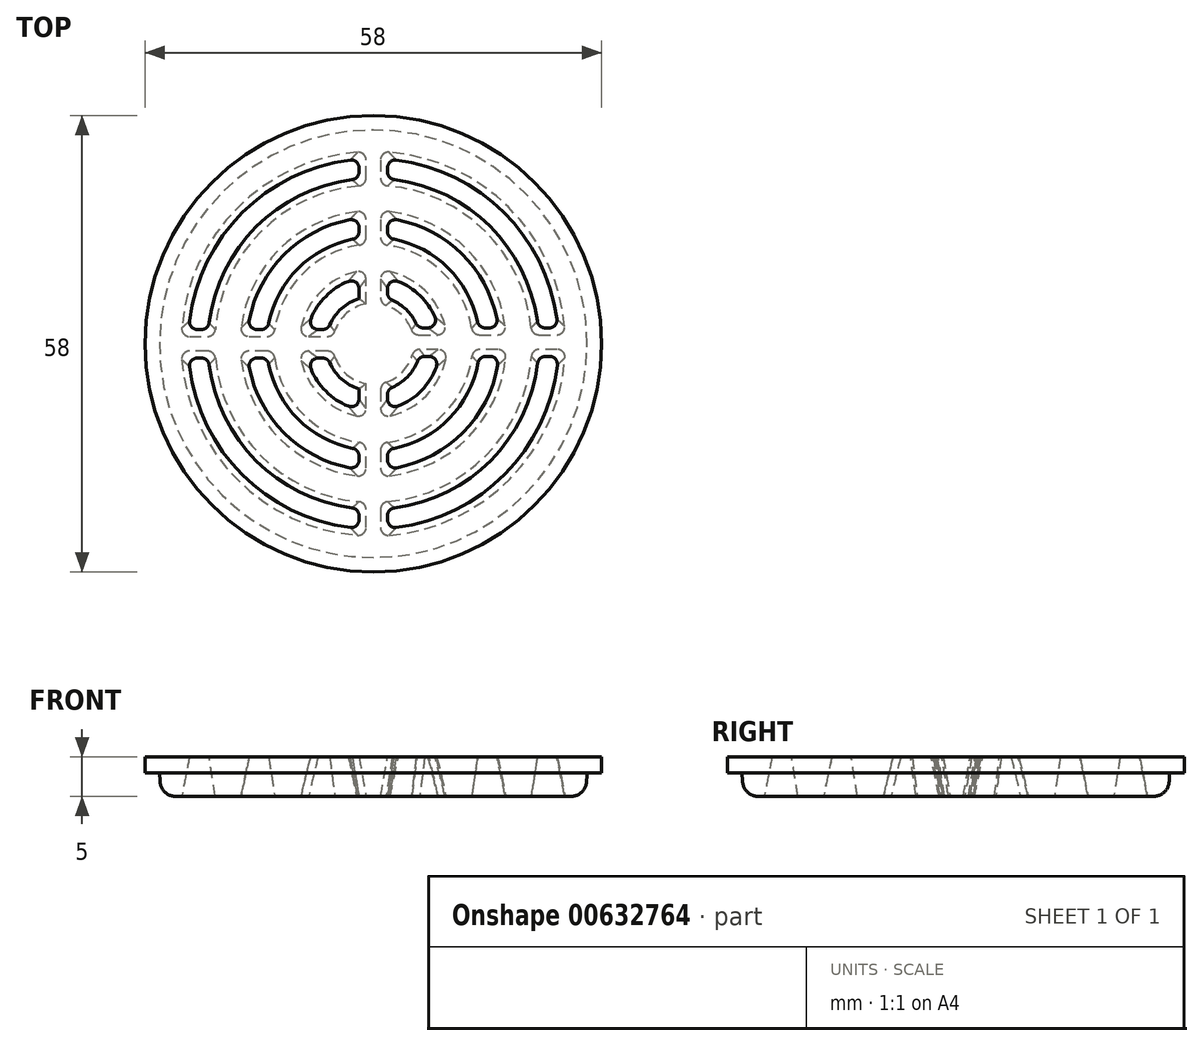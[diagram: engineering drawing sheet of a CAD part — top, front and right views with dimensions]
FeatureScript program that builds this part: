
annotation { "Feature Type Name" : "Feature", "Feature Type Description" : "" }
export const myFeature = defineFeature(function(context is Context, id is Id, definition is map)
    precondition{}
    {
        {
            var Q0;
            Q0=qCreatedBy(makeId("Top.planeOp"),FACE);
            var sketch = newSketch(context, id + "F0", { "sketchPlane" : qUnion([Q0])});
            skCircle(sketch, "E0", {"center": v(0, 0) * mm, "radius": 27 * mm});
            skSolve(sketch);
        }
        {
            var Q0;
            Q0=makeQuery(id+"F0.imprint","IMPRINT",FACE,{"disambiguationData":[TD([[makeQuery(id+"F0.imprint","IMPRINT",EDGE,{"derivedFrom":sQuery(id+"F0.wireOp",EDGE,"E0")}),1.0]])]});
            extrude(context, id + "F1", {"entities" : qUnion([Q0]), "depth" : 3 * mm, "offsetDistance" : 25 * mm, "hasDraft" : true, "draftAngle" : 3 * degree});
        }
        {
            var Q0;
            Q0=makeQuery(id+"F1.opExtrude","CAP_FACE",FACE,{"disambiguationData":[OSD([sQuery(id+"F0.wireOp",EDGE,"E0")])],"isStart":false});
            var sketch = newSketch(context, id + "F2", { "sketchPlane" : qUnion([Q0])});
            skCircle(sketch, "E1", {"center": v(0, 0) * mm, "radius": 29 * mm});
            skSolve(sketch);
        }
        {
            var Q0;
            Q0 = qSketchRegion(id + "F2", true);
            extrude(context, id + "F3", {"entities" : qUnion([Q0]), "operationType" : NewBodyOperationType.ADD, "depth" : 2 * mm, "offsetDistance" : 25 * mm});
        }
        {
            var Q0;
            Q0=makeQuery(id+"F3.opExtrude","CAP_FACE",FACE,{"disambiguationData":[OSD([sQuery(id+"F2.wireOp",EDGE,"E1")])],"isStart":false});
            var sketch = newSketch(context, id + "F4", { "sketchPlane" : qUnion([Q0])});
            skArc(sketch, "E2", {"start": v(5.68, 2.02) * mm, "mid": v(4.18, 4.34) * mm, "end": v(1.81, 5.75) * mm});
            skArc(sketch, "E3", {"start": v(8.29, 2.02) * mm, "mid": v(5.95, 6.1) * mm, "end": v(1.81, 8.33) * mm});
            skArc(sketch, "E4", {"start": v(13.38, 2.02) * mm, "mid": v(9.5, 9.64) * mm, "end": v(1.81, 13.4) * mm});
            skArc(sketch, "E5", {"start": v(15.9, 2.02) * mm, "mid": v(11.26, 11.4) * mm, "end": v(1.81, 15.93) * mm});
            skArc(sketch, "E6", {"start": v(1.81, -23.46) * mm, "mid": v(16.71, -16.56) * mm, "end": v(23.47, -1.6) * mm});
            skArc(sketch, "E7", {"start": v(20.93, 2.02) * mm, "mid": v(14.8, 14.94) * mm, "end": v(1.81, 20.95) * mm});
            skLineSegment(sketch, "E8.left", {"start": v(-1.81, 15.93) * mm, "end": v(-1.81, 13.4) * mm});
            skLineSegment(sketch, "E8.right", {"start": v(1.81, 15.93) * mm, "end": v(1.81, 13.4) * mm});
            skLineSegment(sketch, "E9.bottom", {"start": v(-5.75, 1.81) * mm, "end": v(-8.33, 1.81) * mm});
            skLineSegment(sketch, "E9.top", {"start": v(-5.75, -1.81) * mm, "end": v(-8.33, -1.81) * mm});
            skLineSegment(sketch, "E10.left", {"start": v(-1.81, -5.75) * mm, "end": v(-1.81, -8.33) * mm});
            skLineSegment(sketch, "E10.right", {"start": v(1.81, -5.75) * mm, "end": v(1.81, -8.33) * mm});
            skLineSegment(sketch, "E11.bottom", {"start": v(5.81, -1.6) * mm, "end": v(8.38, -1.6) * mm});
            skLineSegment(sketch, "E11.top", {"start": v(5.68, 2.02) * mm, "end": v(8.29, 2.02) * mm});
            skArc(sketch, "E12.trimOffspring", {"start": v(1.81, -20.95) * mm, "mid": v(14.94, -14.8) * mm, "end": v(20.97, -1.6) * mm});
            skArc(sketch, "E13.trimOffspring", {"start": v(1.81, -15.93) * mm, "mid": v(11.4, -11.26) * mm, "end": v(15.95, -1.6) * mm});
            skArc(sketch, "E14.trimOffspring", {"start": v(1.81, -13.4) * mm, "mid": v(9.64, -9.5) * mm, "end": v(13.43, -1.6) * mm});
            skArc(sketch, "E15.trimOffspring", {"start": v(1.81, -8.33) * mm, "mid": v(6.1, -5.95) * mm, "end": v(8.38, -1.6) * mm});
            skArc(sketch, "E16.trimOffspring", {"start": v(1.81, -5.75) * mm, "mid": v(4.34, -4.19) * mm, "end": v(5.81, -1.6) * mm});
            skLineSegment(sketch, "E17.trimOffspring", {"start": v(1.81, -13.4) * mm, "end": v(1.81, -15.93) * mm});
            skLineSegment(sketch, "E18.trimOffspring", {"start": v(-1.81, -13.4) * mm, "end": v(-1.81, -15.93) * mm});
            skLineSegment(sketch, "E19.trimOffspring", {"start": v(-1.81, -20.95) * mm, "end": v(-1.81, -23.46) * mm});
            skLineSegment(sketch, "E20.trimOffspring", {"start": v(1.81, -20.95) * mm, "end": v(1.81, -23.46) * mm});
            skLineSegment(sketch, "E21.trimOffspring", {"start": v(13.43, -1.6) * mm, "end": v(15.95, -1.6) * mm});
            skLineSegment(sketch, "E22.trimOffspring", {"start": v(13.38, 2.02) * mm, "end": v(15.9, 2.02) * mm});
            skLineSegment(sketch, "E23.trimOffspring", {"start": v(20.93, 2.02) * mm, "end": v(23.44, 2.02) * mm});
            skLineSegment(sketch, "E24.trimOffspring", {"start": v(20.97, -1.6) * mm, "end": v(23.47, -1.6) * mm});
            skArc(sketch, "E25.trimOffspring", {"start": v(-5.75, -1.81) * mm, "mid": v(-4.26, -4.26) * mm, "end": v(-1.81, -5.75) * mm});
            skArc(sketch, "E26.trimOffspring", {"start": v(-8.33, -1.81) * mm, "mid": v(-6.03, -6.03) * mm, "end": v(-1.81, -8.33) * mm});
            skLineSegment(sketch, "E27.trimOffspring", {"start": v(-13.4, -1.81) * mm, "end": v(-15.93, -1.81) * mm});
            skLineSegment(sketch, "E28.trimOffspring", {"start": v(-13.4, 1.81) * mm, "end": v(-15.93, 1.81) * mm});
            skLineSegment(sketch, "E29.trimOffspring", {"start": v(-20.95, -1.81) * mm, "end": v(-23.46, -1.81) * mm});
            skLineSegment(sketch, "E30.trimOffspring", {"start": v(-20.95, 1.81) * mm, "end": v(-23.46, 1.81) * mm});
            skArc(sketch, "E31.trimOffspring", {"start": v(-15.93, -1.81) * mm, "mid": v(-11.33, -11.33) * mm, "end": v(-1.81, -15.93) * mm});
            skArc(sketch, "E32.trimOffspring", {"start": v(-13.4, -1.81) * mm, "mid": v(-9.57, -9.57) * mm, "end": v(-1.81, -13.4) * mm});
            skArc(sketch, "E33.trimOffspring", {"start": v(-20.95, -1.81) * mm, "mid": v(-14.87, -14.87) * mm, "end": v(-1.81, -20.95) * mm});
            skArc(sketch, "E34.trimOffspring", {"start": v(-23.46, -1.81) * mm, "mid": v(-16.64, -16.64) * mm, "end": v(-1.81, -23.46) * mm});
            skArc(sketch, "E35", {"start": v(23.44, 2.02) * mm, "mid": v(16.56, 16.71) * mm, "end": v(1.81, 23.46) * mm});
            skLineSegment(sketch, "E36", {"start": v(-1.81, 20.95) * mm, "end": v(-1.81, 23.46) * mm});
            skLineSegment(sketch, "E37", {"start": v(1.81, 20.95) * mm, "end": v(1.81, 23.46) * mm});
            skArc(sketch, "E38.trimOffspring", {"start": v(-1.81, 20.95) * mm, "mid": v(-14.87, 14.87) * mm, "end": v(-20.95, 1.81) * mm});
            skArc(sketch, "E39.trimOffspring", {"start": v(-1.81, 23.46) * mm, "mid": v(-16.64, 16.64) * mm, "end": v(-23.46, 1.81) * mm});
            skArc(sketch, "E40.trimOffspring", {"start": v(-1.81, 15.93) * mm, "mid": v(-11.33, 11.33) * mm, "end": v(-15.93, 1.81) * mm});
            skArc(sketch, "E41.trimOffspring", {"start": v(-1.81, 13.4) * mm, "mid": v(-9.57, 9.57) * mm, "end": v(-13.4, 1.81) * mm});
            skLineSegment(sketch, "E42.trimOffspring", {"start": v(1.81, 8.33) * mm, "end": v(1.81, 5.75) * mm});
            skLineSegment(sketch, "E43.trimOffspring", {"start": v(-1.81, 8.33) * mm, "end": v(-1.81, 5.75) * mm});
            skArc(sketch, "E44.trimOffspring", {"start": v(-1.81, 5.75) * mm, "mid": v(-4.26, 4.26) * mm, "end": v(-5.75, 1.81) * mm});
            skArc(sketch, "E45.trimOffspring", {"start": v(-1.81, 8.33) * mm, "mid": v(-6.03, 6.03) * mm, "end": v(-8.33, 1.81) * mm});
            skSolve(sketch);
        }
        {
            var Q0;
            Q0 = qSketchRegion(id + "F4", true);
            extrude(context, id + "F5", {"entities" : qUnion([Q0]), "operationType" : NewBodyOperationType.REMOVE, "oppositeDirection" : true, "depth" : 25 * mm, "offsetDistance" : 25 * mm, "hasDraft" : true, "draftAngle" : 10 * degree});
        }
        {
            var Q0;
            Q0=makeQuery(id+"F5.boolean.opBoolean","COPY",EDGE,{"derivedFrom":makeQuery(id+"F5.opExtrude","SWEPT_EDGE",EDGE,{"disambiguationData":[OSD([sQuery(id+"F4.wireOp",EDGE,"E18.trimOffspring"),sQuery(id+"F4.wireOp",EDGE,"E31.trimOffspring")])]})});
            var Q1;
            Q1=makeQuery(id+"F5.boolean.opBoolean","COPY",EDGE,{"derivedFrom":makeQuery(id+"F5.opExtrude","SWEPT_EDGE",EDGE,{"disambiguationData":[OSD([sQuery(id+"F4.wireOp",EDGE,"E18.trimOffspring"),sQuery(id+"F4.wireOp",EDGE,"E32.trimOffspring")])]})});
            var Q2;
            Q2=makeQuery(id+"F5.boolean.opBoolean","COPY",EDGE,{"derivedFrom":makeQuery(id+"F5.opExtrude","SWEPT_EDGE",EDGE,{"disambiguationData":[OSD([sQuery(id+"F4.wireOp",EDGE,"E27.trimOffspring"),sQuery(id+"F4.wireOp",EDGE,"E32.trimOffspring")])]})});
            var Q3;
            Q3=makeQuery(id+"F5.boolean.opBoolean","COPY",EDGE,{"derivedFrom":makeQuery(id+"F5.opExtrude","SWEPT_EDGE",EDGE,{"disambiguationData":[OSD([sQuery(id+"F4.wireOp",EDGE,"E27.trimOffspring"),sQuery(id+"F4.wireOp",EDGE,"E31.trimOffspring")])]})});
            var Q4;
            Q4=makeQuery(id+"F5.boolean.opBoolean","COPY",EDGE,{"derivedFrom":makeQuery(id+"F5.opExtrude","SWEPT_EDGE",EDGE,{"disambiguationData":[OSD([sQuery(id+"F4.wireOp",EDGE,"E19.trimOffspring"),sQuery(id+"F4.wireOp",EDGE,"E33.trimOffspring")])]})});
            var Q5;
            Q5=makeQuery(id+"F5.boolean.opBoolean","COPY",EDGE,{"derivedFrom":makeQuery(id+"F5.opExtrude","SWEPT_EDGE",EDGE,{"disambiguationData":[OSD([sQuery(id+"F4.wireOp",EDGE,"E19.trimOffspring"),sQuery(id+"F4.wireOp",EDGE,"E34.trimOffspring")])]})});
            var Q6;
            Q6=makeQuery(id+"F5.boolean.opBoolean","COPY",EDGE,{"derivedFrom":makeQuery(id+"F5.opExtrude","SWEPT_EDGE",EDGE,{"disambiguationData":[OSD([sQuery(id+"F4.wireOp",EDGE,"E29.trimOffspring"),sQuery(id+"F4.wireOp",EDGE,"E34.trimOffspring")])]})});
            var Q7;
            Q7=makeQuery(id+"F5.boolean.opBoolean","COPY",EDGE,{"derivedFrom":makeQuery(id+"F5.opExtrude","SWEPT_EDGE",EDGE,{"disambiguationData":[OSD([sQuery(id+"F4.wireOp",EDGE,"E29.trimOffspring"),sQuery(id+"F4.wireOp",EDGE,"E33.trimOffspring")])]})});
            var Q8;
            Q8=makeQuery(id+"F5.boolean.opBoolean","COPY",EDGE,{"derivedFrom":makeQuery(id+"F5.opExtrude","SWEPT_EDGE",EDGE,{"disambiguationData":[OSD([sQuery(id+"F4.wireOp",EDGE,"E10.left"),sQuery(id+"F4.wireOp",EDGE,"E26.trimOffspring")])]})});
            var Q9;
            Q9=makeQuery(id+"F5.boolean.opBoolean","TWEAK_EDGE",EDGE,{"disambiguationData":[OD(0.0)],"derivedFrom":[makeQuery(id+"F5.opExtrude","SWEPT_EDGE",EDGE,{"disambiguationData":[OSD([sQuery(id+"F4.wireOp",EDGE,"E10.left"),sQuery(id+"F4.wireOp",EDGE,"E25.trimOffspring")])]}),makeQuery(id+"F5.opExtrude","SWEPT_EDGE",EDGE,{"disambiguationData":[OSD([sQuery(id+"F4.wireOp",EDGE,"E43.trimOffspring"),sQuery(id+"F4.wireOp",EDGE,"E44.trimOffspring")])]})]});
            var Q10;
            Q10=makeQuery(id+"F5.boolean.opBoolean","COPY",EDGE,{"derivedFrom":makeQuery(id+"F5.opExtrude","SWEPT_EDGE",EDGE,{"disambiguationData":[OSD([sQuery(id+"F4.wireOp",EDGE,"E9.top"),sQuery(id+"F4.wireOp",EDGE,"E25.trimOffspring")])]})});
            var Q11;
            Q11=makeQuery(id+"F5.boolean.opBoolean","COPY",EDGE,{"derivedFrom":makeQuery(id+"F5.opExtrude","SWEPT_EDGE",EDGE,{"disambiguationData":[OSD([sQuery(id+"F4.wireOp",EDGE,"E9.top"),sQuery(id+"F4.wireOp",EDGE,"E26.trimOffspring")])]})});
            var Q12;
            Q12=makeQuery(id+"F5.boolean.opBoolean","COPY",EDGE,{"derivedFrom":makeQuery(id+"F5.opExtrude","SWEPT_EDGE",EDGE,{"disambiguationData":[OSD([sQuery(id+"F4.wireOp",EDGE,"E6"),sQuery(id+"F4.wireOp",EDGE,"E20.trimOffspring")])]})});
            var Q13;
            Q13=makeQuery(id+"F5.boolean.opBoolean","COPY",EDGE,{"derivedFrom":makeQuery(id+"F5.opExtrude","SWEPT_EDGE",EDGE,{"disambiguationData":[OSD([sQuery(id+"F4.wireOp",EDGE,"E12.trimOffspring"),sQuery(id+"F4.wireOp",EDGE,"E20.trimOffspring")])]})});
            var Q14;
            Q14=makeQuery(id+"F5.boolean.opBoolean","COPY",EDGE,{"derivedFrom":makeQuery(id+"F5.opExtrude","SWEPT_EDGE",EDGE,{"disambiguationData":[OSD([sQuery(id+"F4.wireOp",EDGE,"E6"),sQuery(id+"F4.wireOp",EDGE,"E24.trimOffspring")])]})});
            var Q15;
            Q15=makeQuery(id+"F5.boolean.opBoolean","COPY",EDGE,{"derivedFrom":makeQuery(id+"F5.opExtrude","SWEPT_EDGE",EDGE,{"disambiguationData":[OSD([sQuery(id+"F4.wireOp",EDGE,"E12.trimOffspring"),sQuery(id+"F4.wireOp",EDGE,"E24.trimOffspring")])]})});
            var Q16;
            Q16=makeQuery(id+"F5.boolean.opBoolean","COPY",EDGE,{"derivedFrom":makeQuery(id+"F5.opExtrude","SWEPT_EDGE",EDGE,{"disambiguationData":[OSD([sQuery(id+"F4.wireOp",EDGE,"E13.trimOffspring"),sQuery(id+"F4.wireOp",EDGE,"E21.trimOffspring")])]})});
            var Q17;
            Q17=makeQuery(id+"F5.boolean.opBoolean","COPY",EDGE,{"derivedFrom":makeQuery(id+"F5.opExtrude","SWEPT_EDGE",EDGE,{"disambiguationData":[OSD([sQuery(id+"F4.wireOp",EDGE,"E14.trimOffspring"),sQuery(id+"F4.wireOp",EDGE,"E21.trimOffspring")])]})});
            var Q18;
            Q18=makeQuery(id+"F5.boolean.opBoolean","COPY",EDGE,{"derivedFrom":makeQuery(id+"F5.opExtrude","SWEPT_EDGE",EDGE,{"disambiguationData":[OSD([sQuery(id+"F4.wireOp",EDGE,"E11.bottom"),sQuery(id+"F4.wireOp",EDGE,"E15.trimOffspring")])]})});
            var Q19;
            Q19=makeQuery(id+"F5.boolean.opBoolean","COPY",EDGE,{"derivedFrom":makeQuery(id+"F5.opExtrude","SWEPT_EDGE",EDGE,{"disambiguationData":[OSD([sQuery(id+"F4.wireOp",EDGE,"E11.bottom"),sQuery(id+"F4.wireOp",EDGE,"E16.trimOffspring")])]})});
            var Q20;
            Q20=makeQuery(id+"F5.boolean.opBoolean","COPY",EDGE,{"derivedFrom":makeQuery(id+"F5.opExtrude","SWEPT_EDGE",EDGE,{"disambiguationData":[OSD([sQuery(id+"F4.wireOp",EDGE,"E10.right"),sQuery(id+"F4.wireOp",EDGE,"E15.trimOffspring")])]})});
            var Q21;
            Q21=makeQuery(id+"F5.boolean.opBoolean","COPY",EDGE,{"derivedFrom":makeQuery(id+"F5.opExtrude","SWEPT_EDGE",EDGE,{"disambiguationData":[OSD([sQuery(id+"F4.wireOp",EDGE,"E10.right"),sQuery(id+"F4.wireOp",EDGE,"E16.trimOffspring")])]})});
            var Q22;
            Q22=makeQuery(id+"F5.boolean.opBoolean","COPY",EDGE,{"derivedFrom":makeQuery(id+"F5.opExtrude","SWEPT_EDGE",EDGE,{"disambiguationData":[OSD([sQuery(id+"F4.wireOp",EDGE,"E2"),sQuery(id+"F4.wireOp",EDGE,"E11.top")])]})});
            var Q23;
            Q23=makeQuery(id+"F5.boolean.opBoolean","COPY",EDGE,{"derivedFrom":makeQuery(id+"F5.opExtrude","SWEPT_EDGE",EDGE,{"disambiguationData":[OSD([sQuery(id+"F4.wireOp",EDGE,"E3"),sQuery(id+"F4.wireOp",EDGE,"E11.top")])]})});
            var Q24;
            Q24=makeQuery(id+"F5.boolean.opBoolean","COPY",EDGE,{"derivedFrom":makeQuery(id+"F5.opExtrude","SWEPT_EDGE",EDGE,{"disambiguationData":[OSD([sQuery(id+"F4.wireOp",EDGE,"E4"),sQuery(id+"F4.wireOp",EDGE,"E22.trimOffspring")])]})});
            var Q25;
            Q25=makeQuery(id+"F5.boolean.opBoolean","COPY",EDGE,{"derivedFrom":makeQuery(id+"F5.opExtrude","SWEPT_EDGE",EDGE,{"disambiguationData":[OSD([sQuery(id+"F4.wireOp",EDGE,"E5"),sQuery(id+"F4.wireOp",EDGE,"E22.trimOffspring")])]})});
            var Q26;
            Q26=makeQuery(id+"F5.boolean.opBoolean","COPY",EDGE,{"derivedFrom":makeQuery(id+"F5.opExtrude","SWEPT_EDGE",EDGE,{"disambiguationData":[OSD([sQuery(id+"F4.wireOp",EDGE,"E7"),sQuery(id+"F4.wireOp",EDGE,"E23.trimOffspring")])]})});
            var Q27;
            Q27=makeQuery(id+"F5.boolean.opBoolean","COPY",EDGE,{"derivedFrom":makeQuery(id+"F5.opExtrude","SWEPT_EDGE",EDGE,{"disambiguationData":[OSD([sQuery(id+"F4.wireOp",EDGE,"E23.trimOffspring"),sQuery(id+"F4.wireOp",EDGE,"E35")])]})});
            var Q28;
            Q28=makeQuery(id+"F5.boolean.opBoolean","COPY",EDGE,{"derivedFrom":makeQuery(id+"F5.opExtrude","SWEPT_EDGE",EDGE,{"disambiguationData":[OSD([sQuery(id+"F4.wireOp",EDGE,"E2"),sQuery(id+"F4.wireOp",EDGE,"E42.trimOffspring")])]})});
            var Q29;
            Q29=makeQuery(id+"F5.boolean.opBoolean","COPY",EDGE,{"derivedFrom":makeQuery(id+"F5.opExtrude","SWEPT_EDGE",EDGE,{"disambiguationData":[OSD([sQuery(id+"F4.wireOp",EDGE,"E3"),sQuery(id+"F4.wireOp",EDGE,"E42.trimOffspring")])]})});
            var Q30;
            Q30=makeQuery(id+"F5.boolean.opBoolean","TWEAK_EDGE",EDGE,{"disambiguationData":[OD(1.0)],"derivedFrom":[makeQuery(id+"F5.opExtrude","SWEPT_EDGE",EDGE,{"disambiguationData":[OSD([sQuery(id+"F4.wireOp",EDGE,"E10.left"),sQuery(id+"F4.wireOp",EDGE,"E25.trimOffspring")])]}),makeQuery(id+"F5.opExtrude","SWEPT_EDGE",EDGE,{"disambiguationData":[OSD([sQuery(id+"F4.wireOp",EDGE,"E43.trimOffspring"),sQuery(id+"F4.wireOp",EDGE,"E44.trimOffspring")])]})]});
            var Q31;
            Q31=makeQuery(id+"F5.boolean.opBoolean","COPY",EDGE,{"derivedFrom":makeQuery(id+"F5.opExtrude","SWEPT_EDGE",EDGE,{"disambiguationData":[OSD([sQuery(id+"F4.wireOp",EDGE,"E43.trimOffspring"),sQuery(id+"F4.wireOp",EDGE,"E45.trimOffspring")])]})});
            var Q32;
            Q32=makeQuery(id+"F5.boolean.opBoolean","COPY",EDGE,{"derivedFrom":makeQuery(id+"F5.opExtrude","SWEPT_EDGE",EDGE,{"disambiguationData":[OSD([sQuery(id+"F4.wireOp",EDGE,"E9.bottom"),sQuery(id+"F4.wireOp",EDGE,"E44.trimOffspring")])]})});
            var Q33;
            Q33=makeQuery(id+"F5.boolean.opBoolean","COPY",EDGE,{"derivedFrom":makeQuery(id+"F5.opExtrude","SWEPT_EDGE",EDGE,{"disambiguationData":[OSD([sQuery(id+"F4.wireOp",EDGE,"E9.bottom"),sQuery(id+"F4.wireOp",EDGE,"E45.trimOffspring")])]})});
            var Q34;
            Q34=makeQuery(id+"F5.boolean.opBoolean","COPY",EDGE,{"derivedFrom":makeQuery(id+"F5.opExtrude","SWEPT_EDGE",EDGE,{"disambiguationData":[OSD([sQuery(id+"F4.wireOp",EDGE,"E4"),sQuery(id+"F4.wireOp",EDGE,"E8.right")])]})});
            var Q35;
            Q35=makeQuery(id+"F5.boolean.opBoolean","COPY",EDGE,{"derivedFrom":makeQuery(id+"F5.opExtrude","SWEPT_EDGE",EDGE,{"disambiguationData":[OSD([sQuery(id+"F4.wireOp",EDGE,"E5"),sQuery(id+"F4.wireOp",EDGE,"E8.right")])]})});
            var Q36;
            Q36=makeQuery(id+"F5.boolean.opBoolean","COPY",EDGE,{"derivedFrom":makeQuery(id+"F5.opExtrude","SWEPT_EDGE",EDGE,{"disambiguationData":[OSD([sQuery(id+"F4.wireOp",EDGE,"E7"),sQuery(id+"F4.wireOp",EDGE,"E37")])]})});
            var Q37;
            Q37=makeQuery(id+"F5.boolean.opBoolean","COPY",EDGE,{"derivedFrom":makeQuery(id+"F5.opExtrude","SWEPT_EDGE",EDGE,{"disambiguationData":[OSD([sQuery(id+"F4.wireOp",EDGE,"E35"),sQuery(id+"F4.wireOp",EDGE,"E37")])]})});
            var Q38;
            Q38=makeQuery(id+"F5.boolean.opBoolean","COPY",EDGE,{"derivedFrom":makeQuery(id+"F5.opExtrude","SWEPT_EDGE",EDGE,{"disambiguationData":[OSD([sQuery(id+"F4.wireOp",EDGE,"E36"),sQuery(id+"F4.wireOp",EDGE,"E38.trimOffspring")])]})});
            var Q39;
            Q39=makeQuery(id+"F5.boolean.opBoolean","COPY",EDGE,{"derivedFrom":makeQuery(id+"F5.opExtrude","SWEPT_EDGE",EDGE,{"disambiguationData":[OSD([sQuery(id+"F4.wireOp",EDGE,"E36"),sQuery(id+"F4.wireOp",EDGE,"E39.trimOffspring")])]})});
            var Q40;
            Q40=makeQuery(id+"F5.boolean.opBoolean","COPY",EDGE,{"derivedFrom":makeQuery(id+"F5.opExtrude","SWEPT_EDGE",EDGE,{"disambiguationData":[OSD([sQuery(id+"F4.wireOp",EDGE,"E8.left"),sQuery(id+"F4.wireOp",EDGE,"E41.trimOffspring")])]})});
            var Q41;
            Q41=makeQuery(id+"F5.boolean.opBoolean","COPY",EDGE,{"derivedFrom":makeQuery(id+"F5.opExtrude","SWEPT_EDGE",EDGE,{"disambiguationData":[OSD([sQuery(id+"F4.wireOp",EDGE,"E8.left"),sQuery(id+"F4.wireOp",EDGE,"E40.trimOffspring")])]})});
            var Q42;
            Q42=makeQuery(id+"F5.boolean.opBoolean","COPY",EDGE,{"derivedFrom":makeQuery(id+"F5.opExtrude","SWEPT_EDGE",EDGE,{"disambiguationData":[OSD([sQuery(id+"F4.wireOp",EDGE,"E30.trimOffspring"),sQuery(id+"F4.wireOp",EDGE,"E38.trimOffspring")])]})});
            var Q43;
            Q43=makeQuery(id+"F5.boolean.opBoolean","COPY",EDGE,{"derivedFrom":makeQuery(id+"F5.opExtrude","SWEPT_EDGE",EDGE,{"disambiguationData":[OSD([sQuery(id+"F4.wireOp",EDGE,"E30.trimOffspring"),sQuery(id+"F4.wireOp",EDGE,"E39.trimOffspring")])]})});
            var Q44;
            Q44=makeQuery(id+"F5.boolean.opBoolean","COPY",EDGE,{"derivedFrom":makeQuery(id+"F5.opExtrude","SWEPT_EDGE",EDGE,{"disambiguationData":[OSD([sQuery(id+"F4.wireOp",EDGE,"E28.trimOffspring"),sQuery(id+"F4.wireOp",EDGE,"E40.trimOffspring")])]})});
            var Q45;
            Q45=makeQuery(id+"F5.boolean.opBoolean","COPY",EDGE,{"derivedFrom":makeQuery(id+"F5.opExtrude","SWEPT_EDGE",EDGE,{"disambiguationData":[OSD([sQuery(id+"F4.wireOp",EDGE,"E28.trimOffspring"),sQuery(id+"F4.wireOp",EDGE,"E41.trimOffspring")])]})});
            var Q46;
            Q46=makeQuery(id+"F5.boolean.opBoolean","COPY",EDGE,{"derivedFrom":makeQuery(id+"F5.opExtrude","SWEPT_EDGE",EDGE,{"disambiguationData":[OSD([sQuery(id+"F4.wireOp",EDGE,"E13.trimOffspring"),sQuery(id+"F4.wireOp",EDGE,"E17.trimOffspring")])]})});
            var Q47;
            Q47=makeQuery(id+"F5.boolean.opBoolean","COPY",EDGE,{"derivedFrom":makeQuery(id+"F5.opExtrude","SWEPT_EDGE",EDGE,{"disambiguationData":[OSD([sQuery(id+"F4.wireOp",EDGE,"E14.trimOffspring"),sQuery(id+"F4.wireOp",EDGE,"E17.trimOffspring")])]})});
            fillet(context, id + "F6", {"entities" : qUnion([Q0, Q1, Q2, Q3, Q4, Q5, Q6, Q7, Q8, Q9, Q10, Q11, Q12, Q13, Q14, Q15, Q16, Q17, Q18, Q19, Q20, Q21, Q22, Q23, Q24, Q25, Q26, Q27, Q28, Q29, Q30, Q31, Q32, Q33, Q34, Q35, Q36, Q37, Q38, Q39, Q40, Q41, Q42, Q43, Q44, Q45, Q46, Q47]), "radius" : 1 * mm, "tangentPropagation" : true, "allowEdgeOverflow" : false});
        }
        {
            var Q0;
            Q0=makeQuery(id+"F1.opExtrude","CAP_EDGE",EDGE,{"disambiguationData":[OSD([sQuery(id+"F0.wireOp",EDGE,"E0")])],"isStart":true});
            fillet(context, id + "F7", {"entities" : qUnion([Q0]), "radius" : 2 * mm, "tangentPropagation" : true, "allowEdgeOverflow" : false});
        }
    });
